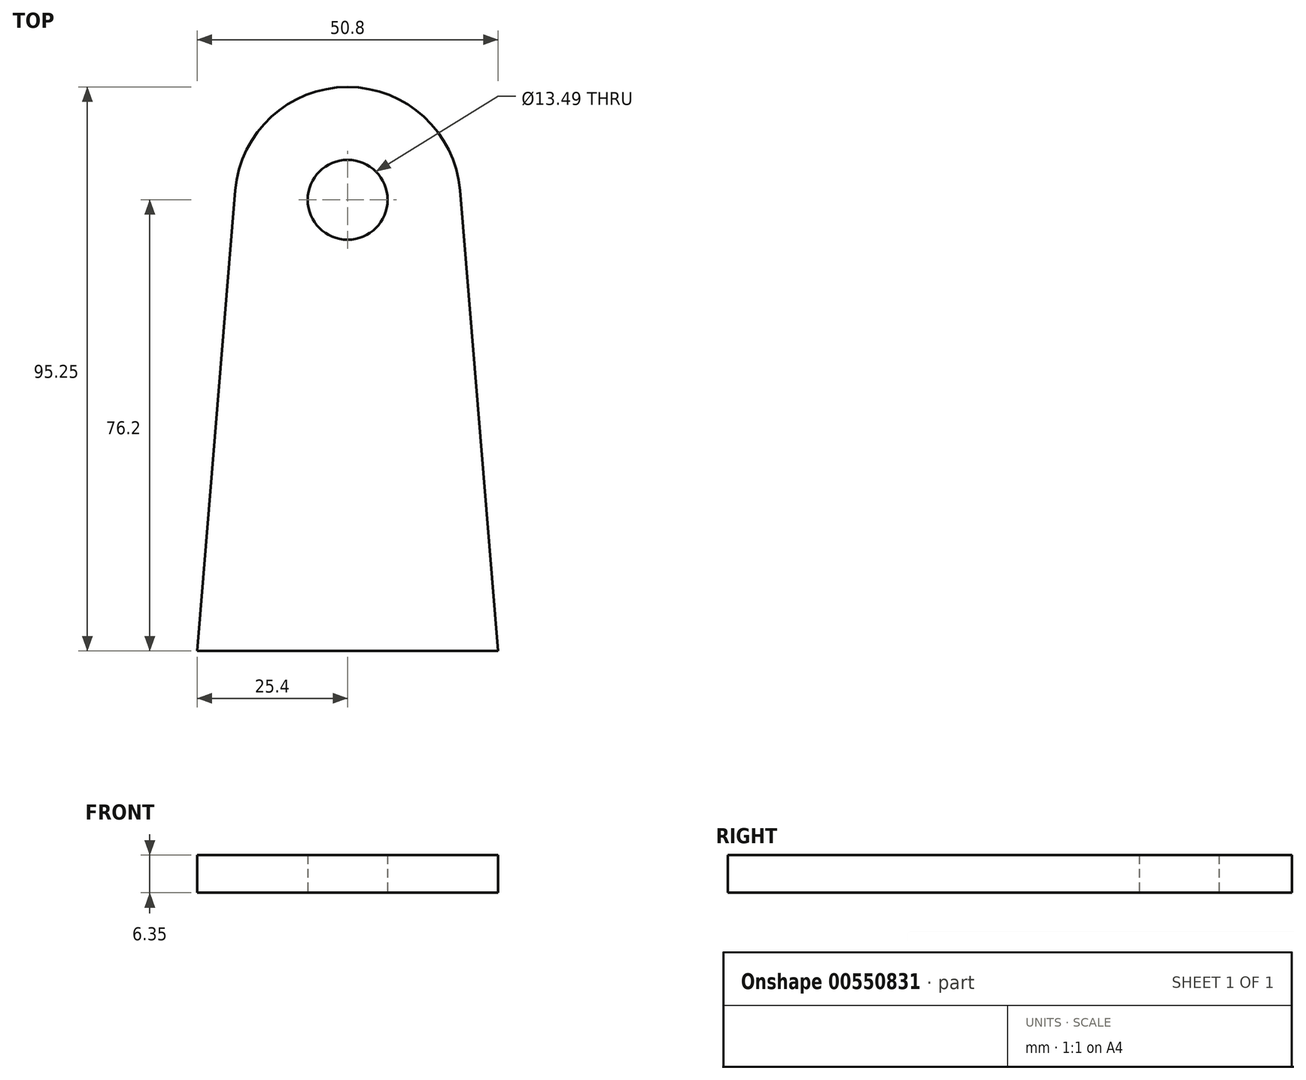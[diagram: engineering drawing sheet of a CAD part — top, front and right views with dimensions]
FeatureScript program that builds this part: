
annotation { "Feature Type Name" : "Feature", "Feature Type Description" : "" }
export const myFeature = defineFeature(function(context is Context, id is Id, definition is map)
    precondition{}
    {
        {
            var Q0;
            Q0=qCreatedBy(makeId("Top.planeOp"),FACE);
            var sketch = newSketch(context, id + "F0", { "sketchPlane" : qUnion([Q0])});
            skCircle(sketch, "E0", {"center": v(0, 0) * mm, "radius": 6.74 * mm});
            skArc(sketch, "E1", {"start": v(18.99, 1.57) * mm, "mid": v(0, 19.05) * mm, "end": v(-18.99, 1.57) * mm});
            skLineSegment(sketch, "E2", {"start": v(0, 0) * mm, "end": v(0, -76.2) * mm, "construction": true});
            skLineSegment(sketch, "E3", {"start": v(25.4, -76.2) * mm, "end": v(-25.4, -76.2) * mm});
            skLineSegment(sketch, "E4", {"start": v(-25.4, -76.2) * mm, "end": v(-18.99, 1.57) * mm});
            skLineSegment(sketch, "E5", {"start": v(18.99, 1.57) * mm, "end": v(25.4, -76.2) * mm});
            skSolve(sketch);
        }
        {
            var Q0;
            Q0 = qSketchRegion(id + "F0", true);
            extrude(context, id + "F1", {"entities" : qUnion([Q0]), "depth" : 6.35 * mm, "offsetDistance" : 25.4 * mm});
        }
    });
